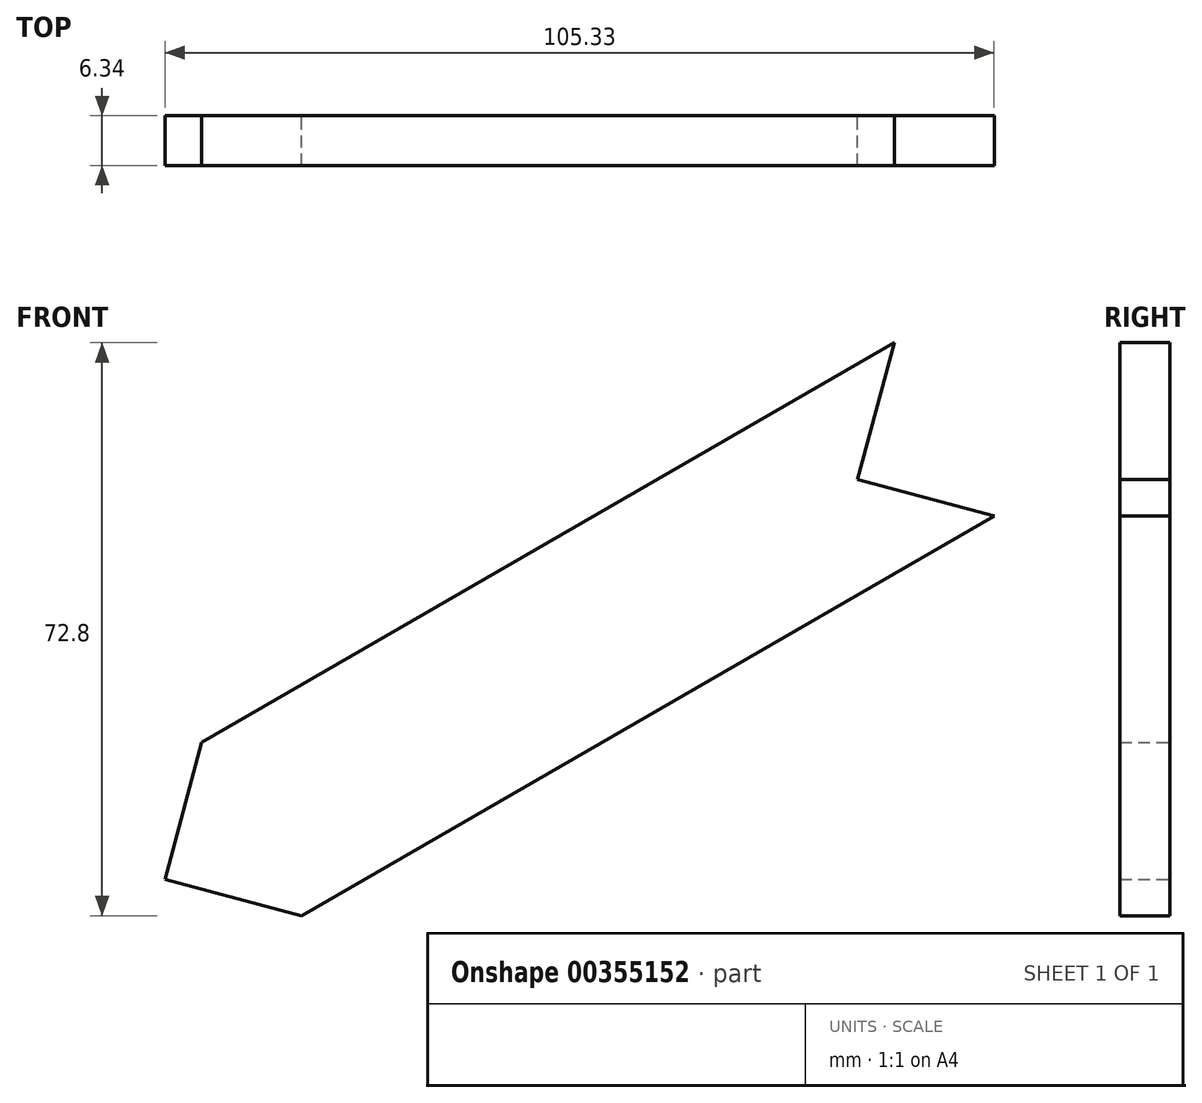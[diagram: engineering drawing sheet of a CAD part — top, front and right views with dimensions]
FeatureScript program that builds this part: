
annotation { "Feature Type Name" : "Feature", "Feature Type Description" : "" }
export const myFeature = defineFeature(function(context is Context, id is Id, definition is map)
    precondition{}
    {
        {
            var Q0;
            Q0=qCreatedBy(makeId("Front.planeOp"),FACE);
            var sketch = newSketch(context, id + "F0", { "sketchPlane" : qUnion([Q0])});
            skLineSegment(sketch, "E0", {"start": v(87.99, -152.4) * mm, "end": v(-263.96, -152.4) * mm});
            skLineSegment(sketch, "E1", {"start": v(-263.96, -152.4) * mm, "end": v(0, 0) * mm});
            skLineSegment(sketch, "E2", {"start": v(0, 0) * mm, "end": v(87.99, -152.4) * mm});
            skLineSegment(sketch, "E3", {"start": v(0, 0) * mm, "end": v(152.4, 87.99) * mm, "construction": true});
            skLineSegment(sketch, "E4", {"start": v(152.4, 87.99) * mm, "end": v(87.99, -152.4) * mm, "construction": true});
            skCircle(sketch, "E5", {"center": v(0, 0) * mm, "radius": 9.53 * mm});
            skCircle(sketch, "E6", {"center": v(0, 0) * mm, "radius": 12.7 * mm});
            skCircle(sketch, "E7", {"center": v(-263.96, -152.4) * mm, "radius": 12.7 * mm});
            skCircle(sketch, "E8", {"center": v(87.99, -152.4) * mm, "radius": 12.7 * mm});
            skLineSegment(sketch, "E9", {"start": v(-6.35, 11) * mm, "end": v(-270.31, -141.4) * mm});
            skLineSegment(sketch, "E10", {"start": v(-263.96, -165.1) * mm, "end": v(87.99, -165.1) * mm});
            skLineSegment(sketch, "E11", {"start": v(98.99, -146.05) * mm, "end": v(11, 6.35) * mm});
            skLineSegment(sketch, "E12", {"start": v(76.99, -158.75) * mm, "end": v(-11, -6.35) * mm});
            skLineSegment(sketch, "E13", {"start": v(-257.61, -163.4) * mm, "end": v(6.35, -11) * mm});
            skLineSegment(sketch, "E14", {"start": v(87.99, -139.7) * mm, "end": v(-263.96, -139.7) * mm});
            skLineSegment(sketch, "E15", {"start": v(87.99, -165.1) * mm, "end": v(109.99, -165.1) * mm});
            skLineSegment(sketch, "E16", {"start": v(98.99, -146.05) * mm, "end": v(109.99, -165.1) * mm});
            skCircle(sketch, "E17", {"center": v(87.99, -152.4) * mm, "radius": 1.59 * mm});
            skCircle(sketch, "E18", {"center": v(-263.96, -152.4) * mm, "radius": 1.59 * mm});
            skLineSegment(sketch, "E19", {"start": v(-270.31, -141.4) * mm, "end": v(-311.36, -165.1) * mm});
            skLineSegment(sketch, "E20", {"start": v(-263.96, -165.1) * mm, "end": v(-311.36, -165.1) * mm});
            skLineSegment(sketch, "E21", {"start": v(-116.34, -52.5) * mm, "end": v(-103.64, -74.5) * mm});
            skLineSegment(sketch, "E22", {"start": v(-116.34, -52.5) * mm, "end": v(-120.98, -69.85) * mm});
            skLineSegment(sketch, "E23", {"start": v(-120.98, -69.85) * mm, "end": v(-103.64, -74.5) * mm});
            skLineSegment(sketch, "E24", {"start": v(-204.32, -103.3) * mm, "end": v(-191.62, -125.3) * mm});
            skLineSegment(sketch, "E25", {"start": v(-191.62, -125.3) * mm, "end": v(-208.97, -120.65) * mm});
            skLineSegment(sketch, "E26", {"start": v(-208.97, -120.65) * mm, "end": v(-204.32, -103.3) * mm});
            skSolve(sketch);
        }
        {
            var Q0;
            {var subQ0=sQuery(id+"F0.wireOp",EDGE,"E26");Q0=makeQuery(id+"F0.imprint","IMPRINT",FACE,{"disambiguationData":[TD([[makeQuery(id+"F0.imprint","IMPRINT",EDGE,{"derivedFrom":subQ0}),-1.0]])]});}
            var Q1;
            {var subQ0=sQuery(id+"F0.wireOp",EDGE,"E25");Q1=makeQuery(id+"F0.imprint","IMPRINT",FACE,{"disambiguationData":[TD([[makeQuery(id+"F0.imprint","IMPRINT",EDGE,{"derivedFrom":subQ0}),-1.0]])]});}
            var Q2;
            {var subQ0=sQuery(id+"F0.wireOp",EDGE,"E23");Q2=makeQuery(id+"F0.imprint","IMPRINT",FACE,{"disambiguationData":[TD([[makeQuery(id+"F0.imprint","IMPRINT",EDGE,{"derivedFrom":subQ0}),-1.0]])]});}
            var Q3;
            {var subQ0=sQuery(id+"F0.wireOp",EDGE,"E22");Q3=makeQuery(id+"F0.imprint","IMPRINT",FACE,{"disambiguationData":[TD([[makeQuery(id+"F0.imprint","IMPRINT",EDGE,{"derivedFrom":subQ0}),-1.0]])]});}
            extrude(context, id + "F1", {"entities" : qUnion([Q0, Q1, Q2, Q3]), "endBound" : BoundingType.SYMMETRIC, "depth" : 6.35 * mm});
        }
    });
